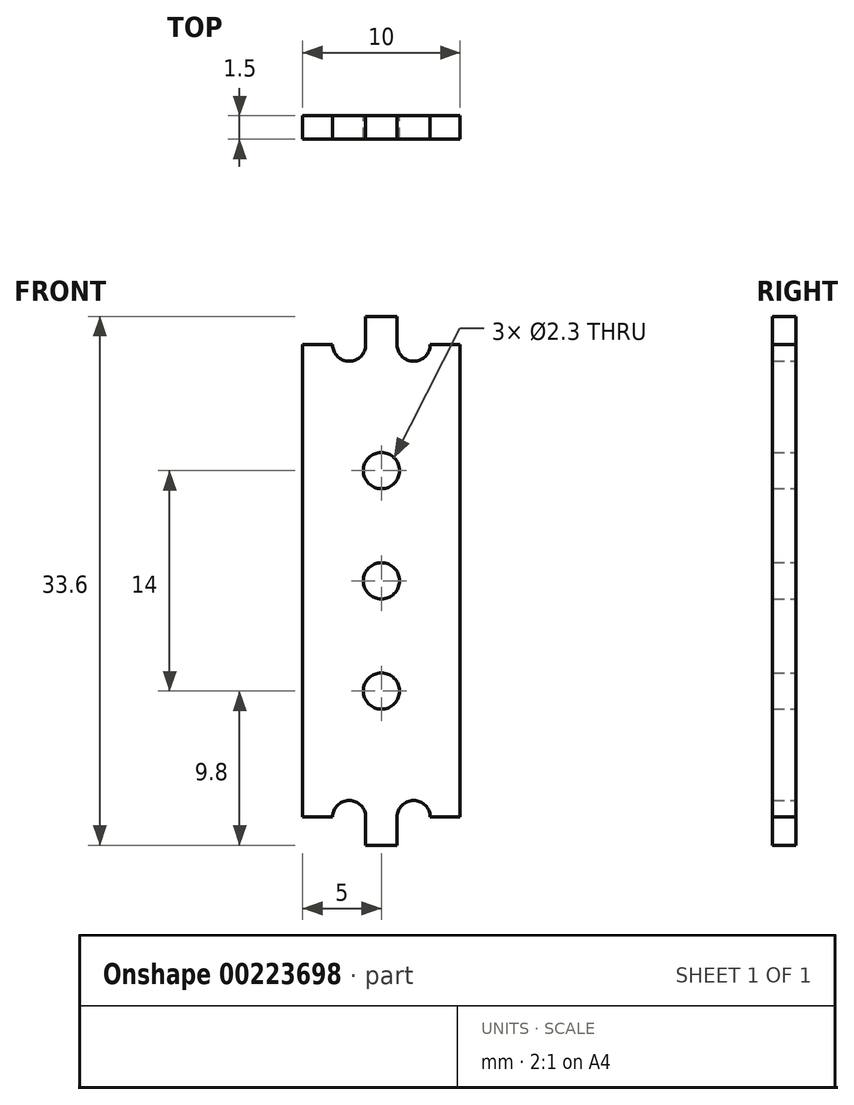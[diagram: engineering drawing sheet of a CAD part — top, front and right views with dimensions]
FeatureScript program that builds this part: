
annotation { "Feature Type Name" : "Feature", "Feature Type Description" : "" }
export const myFeature = defineFeature(function(context is Context, id is Id, definition is map)
    precondition{}
    {
        {
            var Q0;
            Q0=qCreatedBy(makeId("Front.planeOp"),FACE);
            var sketch = newSketch(context, id + "F0", { "sketchPlane" : qUnion([Q0])});
            skCircle(sketch, "E0.MirrorC", {"center": v(0, 7) * mm, "radius": 1.15 * mm});
            skLineSegment(sketch, "E1", {"start": v(-5.38, 0) * mm, "end": v(8.5, 0) * mm, "construction": true});
            skLineSegment(sketch, "E2", {"start": v(0, -6.54) * mm, "end": v(0, 9.4) * mm, "construction": true});
            skCircle(sketch, "E3", {"center": v(0, 0) * mm, "radius": 1.15 * mm});
            skLineSegment(sketch, "E4", {"start": v(-5, 0) * mm, "end": v(-5, 15) * mm});
            skLineSegment(sketch, "E5", {"start": v(-5, 15) * mm, "end": v(-3.1, 15) * mm});
            skLineSegment(sketch, "E6", {"start": v(-1, 15) * mm, "end": v(-1, 16.8) * mm});
            skLineSegment(sketch, "E7", {"start": v(-1, 16.8) * mm, "end": v(0, 16.8) * mm});
            skArc(sketch, "E8", {"start": v(-3.1, 15) * mm, "mid": v(-2.05, 13.95) * mm, "end": v(-1, 15) * mm});
            skLineSegment(sketch, "E9.MirrorCS", {"start": v(5, 0) * mm, "end": v(5, 15) * mm});
            skLineSegment(sketch, "E10.MirrorCS", {"start": v(5, 15) * mm, "end": v(3.1, 15) * mm});
            skArc(sketch, "E11.MirrorCS", {"start": v(3.1, 15) * mm, "mid": v(2.05, 13.95) * mm, "end": v(1, 15) * mm});
            skLineSegment(sketch, "E12.MirrorCS", {"start": v(1, 16.8) * mm, "end": v(0, 16.8) * mm});
            skLineSegment(sketch, "E13.MirrorCS", {"start": v(1, 15) * mm, "end": v(1, 16.8) * mm});
            skLineSegment(sketch, "E14.MirrorCS", {"start": v(-5, 0) * mm, "end": v(-5, -15) * mm});
            skLineSegment(sketch, "E15.MirrorCS", {"start": v(5, 0) * mm, "end": v(5, -15) * mm});
            skLineSegment(sketch, "E16.MirrorCS", {"start": v(1, -15) * mm, "end": v(1, -16.8) * mm});
            skLineSegment(sketch, "E17.MirrorCS", {"start": v(1, -16.8) * mm, "end": v(0, -16.8) * mm});
            skArc(sketch, "E18.MirrorCS", {"start": v(3.1, -15) * mm, "mid": v(2.05, -13.95) * mm, "end": v(1, -15) * mm});
            skLineSegment(sketch, "E19.MirrorCS", {"start": v(5, -15) * mm, "end": v(3.1, -15) * mm});
            skArc(sketch, "E20.MirrorCS", {"start": v(-3.1, -15) * mm, "mid": v(-2.05, -13.95) * mm, "end": v(-1, -15) * mm});
            skLineSegment(sketch, "E21.MirrorCS", {"start": v(-1, -16.8) * mm, "end": v(0, -16.8) * mm});
            skLineSegment(sketch, "E22.MirrorCS", {"start": v(-5, -15) * mm, "end": v(-3.1, -15) * mm});
            skLineSegment(sketch, "E23.MirrorCS", {"start": v(-1, -15) * mm, "end": v(-1, -16.8) * mm});
            skCircle(sketch, "E24.MirrorC", {"center": v(0, -7) * mm, "radius": 1.15 * mm});
            skSolve(sketch);
        }
        {
            var Q0;
            Q0=qSketchRegion(id+"F0",true);
            extrude(context, id + "F1", {"entities" : qUnion([Q0]), "depth" : 1.5 * mm});
        }
    });
